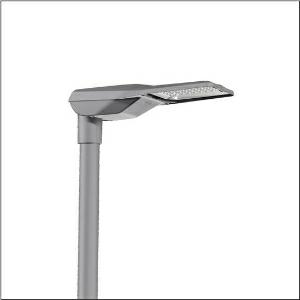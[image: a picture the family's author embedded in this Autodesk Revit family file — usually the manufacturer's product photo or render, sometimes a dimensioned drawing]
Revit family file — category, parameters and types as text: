
# Revit family: streetlight_sl_21_iq_mini___st0_5a_5xe2b41g08hb_4387
name_source: partatom
category: Lighting Fixtures
units: mm (PartAtom-declared; Revit-internal decimal feet)

## family parameters
Cut with Voids When Loaded = No
Host = Face
Light Source = No
Part Type = Normal
Room Calculation Point = No
Round Connector Dimension = Use Diameter
Shared = No

## types (1)
- --- (1 x LED, 9860 lm, 70.9 W, 4000K)
    Apparent Load = 71 VA
    CIE Flux Codes = 41 75 97 100 100
    Color Rendering = 70
    Color Temperature = 4000K
    Default Elevation = 1800 mm
    Description = Streetlight SL 21 iQ mini, mast luminaire, primary light control with lens, of PMMA, primary optical cover: cover, of toughened safety glass, transparent, light distribution: ST0.5a, light emission: direct distribution, primary light characteristic: asymmetric, installation type: post-top, side-entry, LED, High Power LED, rated luminous flux: 9.860lm, luminous efficacy: 139lm/W, light colour: 740, colour temperature: 4000K, control gear: iQ Street-Remote, control: Street-Remote, Auto-Match, Temp-Guard, Lumen-Switch, Night-Set, Smart-Wire, Light-Fading, Desk-Remote (wireless, voltage-free reading and setting of iQ features in the workshop via application-optimized NFC function/RFID function), optimised constant luminous flux control (CLO 2.0), pre-setting: linear dimming characteristic, mains connection: 220..240V, AC, 50/60Hz, start of lifetime: 71W, end of service life: 75W, reduction: 31W, luminaire housing, of diecast aluminium, powder-coated, Siteco® metallic grey (DB 702S), corrosivity category C5 mid according to DIN EN ISO 12944, please order mast flange separately, inclination adjustable: 0°, 5°, 10°, 15°, sealing non-destructively replaceable, multi-level sealing system, length: 628mm, width: 235mm, height: 110mm, mast flange for spigot size: 42mm (side-entry): 5XC10008XM4, 60/48mm (side-entry/post-top): 5XC10108XM2, 76/60mm (side-entry/post-top): 5XC10108XM1, mounting height: 4..8m, protection rating (complete): IP66, insulation class (complete): insulation class II (safety insulation), certification: CE, ENEC, ENEC+, VDE, impact resistance: IK10, permissible operating ambient temperature for outdoor applications: -40..+50°C, standard-compliant lighting for roads and squares, packaging unit: 1 piece

Light Distribution: ST0.5a
    Height = 110 mm
    Lamp = 1 x LED
    Lamp Light Flux = 9860 lm
    Lamp Power = 70.9 W
    Lamp count = 1
    Length = 625 mm
    Luminous efficacy = 139 lm/W
    Manufacturer = Siteco
    ModVariant = No
    Model = 5XE2B41G08HB
    Number of Poles = 1
    OnlyDefault = Yes
    Power Factor = 1
    Product Name = Streetlight SL 21 iQ mini | ST0.5a
    Product group = mast luminaire | pylon top
    ProductGroupID = 6100
    Protection Class = Protection class II
    Protection Degree = IP 66
    RLX_Detail_Level = 1
    RLX_Emergency_Light_Flux = 0 lm
    RLX_Emergency_Type = 0
    RLX_Emergency_Type_DB = No
    RlxData = <blob elided: 37193 chars, md5=b45c9560>
    Socket = socket
    Standby Power = 0 W
    System Light Flux = 9860 lm
    System Power = 71 W
    Type Comments = factory setting: luminous flux: 100 % | dim-lin: 254 | 711 mA
    Type Image = l_1003519.jpg
    URL = http://relux.com
    VarID = @adj_158530
    Voltage = 0 V
    Weight = 0.00 kg
    Width = 234 mm

## geometry (parser evidence)
native form markers: Blend x4, Sweep x10
no freeform markers — native parametric forms only
